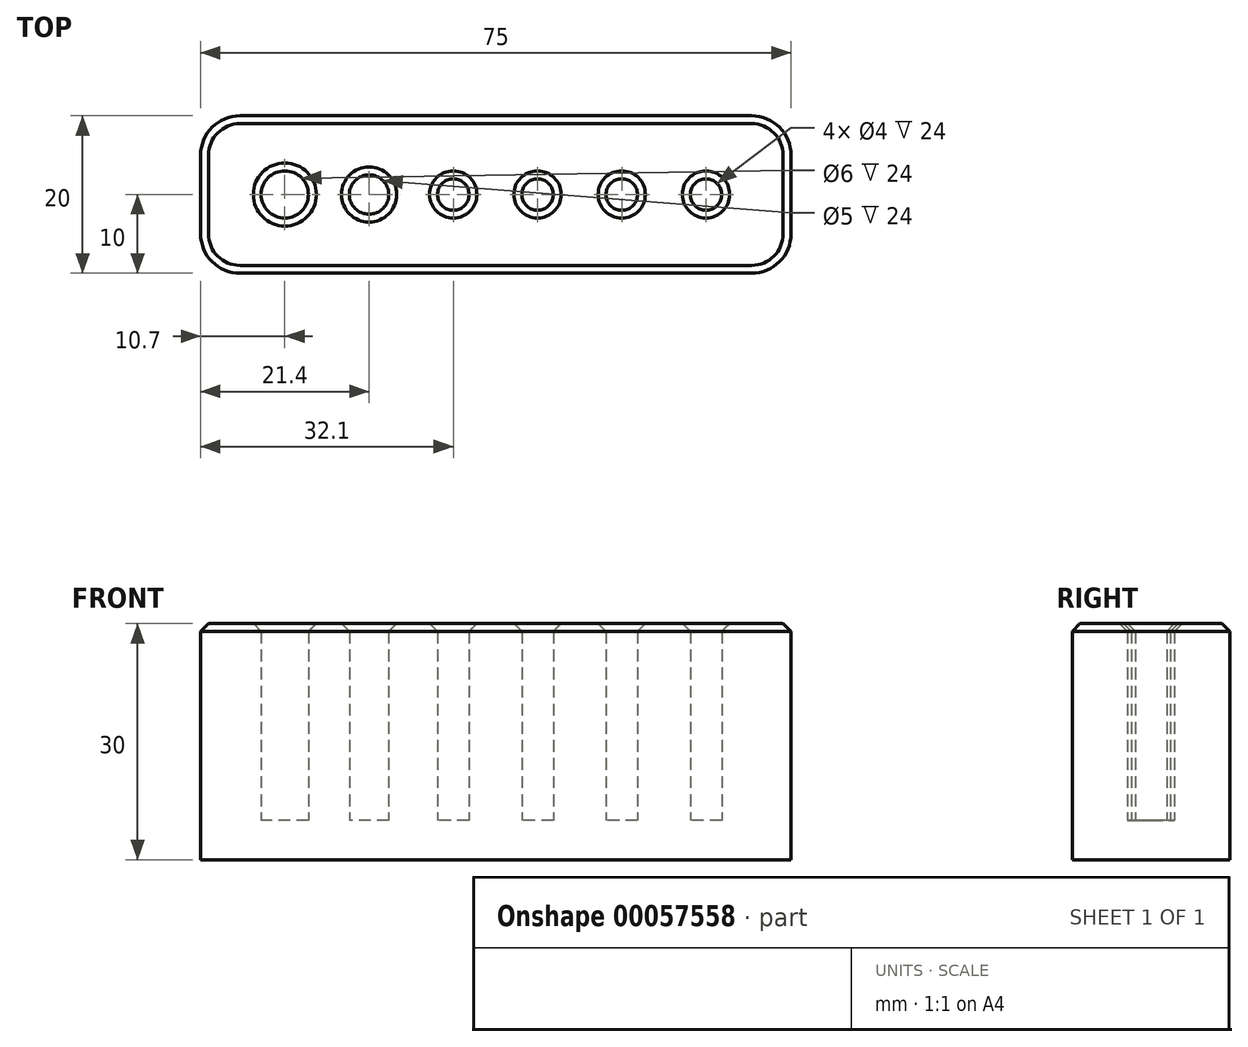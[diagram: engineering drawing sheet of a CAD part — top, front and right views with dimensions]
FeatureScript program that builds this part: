
annotation { "Feature Type Name" : "Feature", "Feature Type Description" : "" }
export const myFeature = defineFeature(function(context is Context, id is Id, definition is map)
    precondition{}
    {
        {
            var Q0;
            Q0=qCreatedBy(makeId("Top.planeOp"),FACE);
            var sketch = newSketch(context, id + "F0", { "sketchPlane" : qUnion([Q0])});
            skLineSegment(sketch, "E0.rect.bottom", {"start": v(37.5, -10) * mm, "end": v(-37.5, -10) * mm});
            skLineSegment(sketch, "E0.rect.top", {"start": v(37.5, 10) * mm, "end": v(-37.5, 10) * mm});
            skLineSegment(sketch, "E0.rect.left", {"start": v(37.5, -10) * mm, "end": v(37.5, 10) * mm});
            skLineSegment(sketch, "E0.rect.right", {"start": v(-37.5, -10) * mm, "end": v(-37.5, 10) * mm});
            skPoint(sketch, "E0.rect.middle", {"position": v(0, 0) * mm});
            skCircle(sketch, "E1", {"center": v(-26.8, 0) * mm, "radius": 3 * mm});
            skCircle(sketch, "E2", {"center": v(-16.1, 0) * mm, "radius": 2.5 * mm});
            skCircle(sketch, "E3", {"center": v(-5.4, 0) * mm, "radius": 2 * mm});
            skCircle(sketch, "E4", {"center": v(5.3, 0) * mm, "radius": 2 * mm});
            skCircle(sketch, "E5", {"center": v(16, 0) * mm, "radius": 2 * mm});
            skCircle(sketch, "E6", {"center": v(26.7, 0) * mm, "radius": 2 * mm});
            skSolve(sketch);
        }
        {
            var Q0;
            Q0 = qSketchRegion(id + "F0", true);
            extrude(context, id + "F1", {"entities" : qUnion([Q0]), "depth" : 30 * mm});
        }
        {
            var Q0;
            Q0=makeQuery(id+"F0.imprint","IMPRINT",FACE,{"disambiguationData":[TD([[makeQuery(id+"F0.imprint","IMPRINT",EDGE,{"derivedFrom":sQuery(id+"F0.wireOp",EDGE,"E1")}),1.0]])]});
            var Q1;
            Q1=makeQuery(id+"F0.imprint","IMPRINT",FACE,{"disambiguationData":[TD([[makeQuery(id+"F0.imprint","IMPRINT",EDGE,{"derivedFrom":sQuery(id+"F0.wireOp",EDGE,"E2")}),1.0]])]});
            var Q2;
            Q2=makeQuery(id+"F0.imprint","IMPRINT",FACE,{"disambiguationData":[TD([[makeQuery(id+"F0.imprint","IMPRINT",EDGE,{"derivedFrom":sQuery(id+"F0.wireOp",EDGE,"E3")}),1.0]])]});
            var Q3;
            Q3=makeQuery(id+"F0.imprint","IMPRINT",FACE,{"disambiguationData":[TD([[makeQuery(id+"F0.imprint","IMPRINT",EDGE,{"derivedFrom":sQuery(id+"F0.wireOp",EDGE,"E4")}),1.0]])]});
            var Q4;
            Q4=makeQuery(id+"F0.imprint","IMPRINT",FACE,{"disambiguationData":[TD([[makeQuery(id+"F0.imprint","IMPRINT",EDGE,{"derivedFrom":sQuery(id+"F0.wireOp",EDGE,"E5")}),1.0]])]});
            var Q5;
            Q5=makeQuery(id+"F0.imprint","IMPRINT",FACE,{"disambiguationData":[TD([[makeQuery(id+"F0.imprint","IMPRINT",EDGE,{"derivedFrom":sQuery(id+"F0.wireOp",EDGE,"E6")}),1.0]])]});
            var Q6;
            Q6=sQuery(id+"F0.wireOp",EDGE,"E1");
            var Q7;
            Q7=sQuery(id+"F0.wireOp",EDGE,"E2");
            var Q8;
            Q8=sQuery(id+"F0.wireOp",EDGE,"E3");
            var Q9;
            Q9=sQuery(id+"F0.wireOp",EDGE,"E6");
            var Q10;
            Q10=sQuery(id+"F0.wireOp",EDGE,"E4");
            extrude(context, id + "F2", {"entities" : qUnion([Q0, Q1, Q2, Q3, Q4, Q5]), "operationType" : NewBodyOperationType.ADD, "surfaceEntities" : qUnion([Q6, Q7, Q8, Q9, Q10]), "depth" : 5 * mm});
        }
        {
            var Q0;
            Q0=makeQuery(id+"F1.opExtrude","SWEPT_EDGE",EDGE,{"disambiguationData":[OSD([sQuery(id+"F0.wireOp",EDGE,"E0.rect.bottom"),sQuery(id+"F0.wireOp",EDGE,"E0.rect.left")])]});
            var Q1;
            Q1=makeQuery(id+"F1.opExtrude","SWEPT_EDGE",EDGE,{"disambiguationData":[OSD([sQuery(id+"F0.wireOp",EDGE,"E0.rect.top"),sQuery(id+"F0.wireOp",EDGE,"E0.rect.left")])]});
            var Q2;
            Q2=makeQuery(id+"F1.opExtrude","SWEPT_EDGE",EDGE,{"disambiguationData":[OSD([sQuery(id+"F0.wireOp",EDGE,"E0.rect.bottom"),sQuery(id+"F0.wireOp",EDGE,"E0.rect.right")])]});
            var Q3;
            Q3=makeQuery(id+"F1.opExtrude","SWEPT_EDGE",EDGE,{"disambiguationData":[OSD([sQuery(id+"F0.wireOp",EDGE,"E0.rect.top"),sQuery(id+"F0.wireOp",EDGE,"E0.rect.right")])]});
            fillet(context, id + "F3", {"entities" : qUnion([Q0, Q1, Q2, Q3]), "radius" : 5 * mm, "tangentPropagation" : true, "allowEdgeOverflow" : false});
        }
        {
            var Q0;
            Q0=makeQuery(id+"F1.opExtrude","CAP_EDGE",EDGE,{"disambiguationData":[OSD([sQuery(id+"F0.wireOp",EDGE,"E1")])],"isStart":false});
            var Q1;
            Q1=makeQuery(id+"F1.opExtrude","CAP_EDGE",EDGE,{"disambiguationData":[OSD([sQuery(id+"F0.wireOp",EDGE,"E2")])],"isStart":false});
            var Q2;
            Q2=makeQuery(id+"F1.opExtrude","CAP_EDGE",EDGE,{"disambiguationData":[OSD([sQuery(id+"F0.wireOp",EDGE,"E3")])],"isStart":false});
            var Q3;
            Q3=makeQuery(id+"F1.opExtrude","CAP_EDGE",EDGE,{"disambiguationData":[OSD([sQuery(id+"F0.wireOp",EDGE,"E4")])],"isStart":false});
            var Q4;
            Q4=makeQuery(id+"F1.opExtrude","CAP_EDGE",EDGE,{"disambiguationData":[OSD([sQuery(id+"F0.wireOp",EDGE,"E5")])],"isStart":false});
            var Q5;
            Q5=makeQuery(id+"F1.opExtrude","CAP_EDGE",EDGE,{"disambiguationData":[OSD([sQuery(id+"F0.wireOp",EDGE,"E6")])],"isStart":false});
            var Q6;
            Q6=makeQuery(id+"F1.opExtrude","CAP_EDGE",EDGE,{"disambiguationData":[OSD([sQuery(id+"F0.wireOp",EDGE,"E0.rect.bottom")])],"isStart":false});
            chamfer(context, id + "F4", {"entities" : qUnion([Q0, Q1, Q2, Q3, Q4, Q5, Q6]), "width" : 1 * mm, "tangentPropagation" : true});
        }
    });
